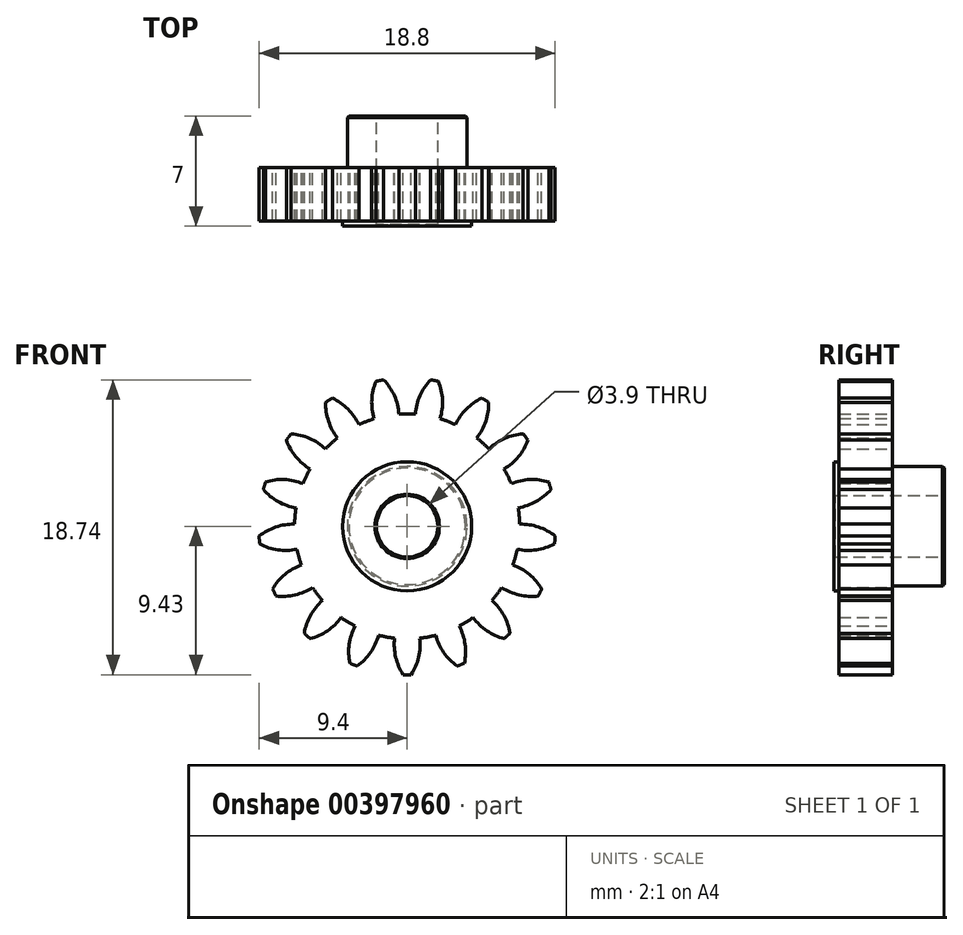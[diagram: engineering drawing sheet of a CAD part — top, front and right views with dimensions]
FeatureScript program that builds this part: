
annotation { "Feature Type Name" : "Feature", "Feature Type Description" : "" }
export const myFeature = defineFeature(function(context is Context, id is Id, definition is map)
    precondition{}
    {
        {
            var Q0;
            Q0=qCreatedBy(makeId("Front.planeOp"),FACE);
            var sketch = newSketch(context, id + "F0", { "sketchPlane" : qUnion([Q0])});
            skArc(sketch, "E0", {"start": v(-7.05, 1.17) * mm, "mid": v(-7.12, 0.66) * mm, "end": v(-7.15, 0.14) * mm});
            skLineSegment(sketch, "E1", {"start": v(-1.73, 9.26) * mm, "end": v(-1.31, 7.03) * mm});
            skLineSegment(sketch, "E2", {"start": v(1.73, 9.26) * mm, "end": v(1.31, 7.03) * mm});
            skLineSegment(sketch, "E3.1.0", {"start": v(9.06, 2.58) * mm, "end": v(6.88, 1.96) * mm});
            skLineSegment(sketch, "E3.1.1", {"start": v(9.38, -0.87) * mm, "end": v(7.12, -0.66) * mm});
            skArc(sketch, "E3.1.2", {"start": v(-7.37, 5.88) * mm, "mid": v(-7.52, 5.68) * mm, "end": v(-7.67, 5.48) * mm});
            skLineSegment(sketch, "E3.2.0", {"start": v(4.96, 8.01) * mm, "end": v(3.76, 6.08) * mm});
            skLineSegment(sketch, "E3.2.1", {"start": v(7.52, 5.68) * mm, "end": v(5.7, 4.3) * mm});
            skLineSegment(sketch, "E4.1.0", {"start": v(-8.44, -4.2) * mm, "end": v(-6.4, -3.19) * mm});
            skLineSegment(sketch, "E4.1.1", {"start": v(-9.38, -0.87) * mm, "end": v(-7.12, -0.66) * mm});
            skLineSegment(sketch, "E4.1.2", {"start": v(-9.07, 2.58) * mm, "end": v(-6.88, 1.96) * mm});
            skLineSegment(sketch, "E4.1.3", {"start": v(-7.52, 5.68) * mm, "end": v(-5.7, 4.3) * mm});
            skLineSegment(sketch, "E4.1.4", {"start": v(-4.96, 8.01) * mm, "end": v(-3.76, 6.08) * mm});
            skLineSegment(sketch, "E4.2.0", {"start": v(8.44, -4.2) * mm, "end": v(6.4, -3.19) * mm});
            skLineSegment(sketch, "E4.2.1", {"start": v(6.35, -6.96) * mm, "end": v(4.82, -5.28) * mm});
            skLineSegment(sketch, "E4.2.2", {"start": v(3.4, -8.79) * mm, "end": v(2.58, -6.67) * mm});
            skLineSegment(sketch, "E4.2.3", {"start": v(0, -9.42) * mm, "end": v(0, -7.15) * mm});
            skLineSegment(sketch, "E4.2.4", {"start": v(-3.4, -8.79) * mm, "end": v(-2.58, -6.67) * mm});
            skLineSegment(sketch, "E4.2.5", {"start": v(-6.35, -6.97) * mm, "end": v(-4.82, -5.28) * mm});
            skPoint(sketch, "E5", {"position": v(-2.1, 6.84) * mm});
            skPoint(sketch, "E6", {"position": v(0.52, 7.13) * mm});
            skPoint(sketch, "E7", {"position": v(3.06, 6.46) * mm});
            skPoint(sketch, "E8", {"position": v(5.19, 4.92) * mm});
            skPoint(sketch, "E9", {"position": v(6.61, 2.71) * mm});
            skPoint(sketch, "E10", {"position": v(6.72, -2.45) * mm});
            skPoint(sketch, "E11", {"position": v(5.38, -4.71) * mm});
            skPoint(sketch, "E12", {"position": v(3.31, -6.34) * mm});
            skPoint(sketch, "E13", {"position": v(0.8, -7.1) * mm});
            skPoint(sketch, "E14", {"position": v(-1.82, -6.91) * mm});
            skPoint(sketch, "E15", {"position": v(-4.2, -5.8) * mm});
            skPoint(sketch, "E16", {"position": v(-6, -3.88) * mm});
            skPoint(sketch, "E17", {"position": v(-7, -1.45) * mm});
            skPoint(sketch, "E18", {"position": v(-7.05, 1.17) * mm});
            skPoint(sketch, "E19", {"position": v(-6.15, 3.64) * mm});
            skPoint(sketch, "E20", {"position": v(-4.42, 5.62) * mm});
            skPoint(sketch, "E21", {"position": v(7.15, 0.14) * mm});
            skPoint(sketch, "E22", {"position": v(1.48, 9.3) * mm});
            skPoint(sketch, "E23", {"position": v(4.75, 8.14) * mm});
            skPoint(sketch, "E24", {"position": v(7.37, 5.88) * mm});
            skPoint(sketch, "E25", {"position": v(9, 2.82) * mm});
            skPoint(sketch, "E26", {"position": v(9.4, -0.62) * mm});
            skPoint(sketch, "E27", {"position": v(8.55, -3.97) * mm});
            skPoint(sketch, "E28", {"position": v(6.53, -6.8) * mm});
            skPoint(sketch, "E29", {"position": v(3.64, -8.7) * mm});
            skPoint(sketch, "E30", {"position": v(0.25, -9.42) * mm});
            skPoint(sketch, "E31", {"position": v(-3.17, -8.88) * mm});
            skPoint(sketch, "E32", {"position": v(-6.16, -7.13) * mm});
            skPoint(sketch, "E33", {"position": v(-8.32, -4.42) * mm});
            skPoint(sketch, "E34", {"position": v(-9.36, -1.12) * mm});
            skPoint(sketch, "E35", {"position": v(-9.13, 2.34) * mm});
            skPoint(sketch, "E36", {"position": v(-7.67, 5.48) * mm});
            skArc(sketch, "E37.MirrorCS", {"start": v(-1.98, 9.22) * mm, "mid": v(-2.24, 8.04) * mm, "end": v(-2.1, 6.84) * mm});
            skArc(sketch, "E38", {"start": v(1.48, 9.3) * mm, "mid": v(0.81, 8.3) * mm, "end": v(0.52, 7.13) * mm});
            skArc(sketch, "E39", {"start": v(4.75, 8.14) * mm, "mid": v(3.76, 7.45) * mm, "end": v(3.06, 6.46) * mm});
            skArc(sketch, "E40", {"start": v(7.37, 5.88) * mm, "mid": v(6.2, 5.6) * mm, "end": v(5.19, 4.92) * mm});
            skArc(sketch, "E41", {"start": v(9, 2.82) * mm, "mid": v(7.8, 2.98) * mm, "end": v(6.61, 2.71) * mm});
            skArc(sketch, "E42", {"start": v(9.4, -0.62) * mm, "mid": v(8.34, -0.04) * mm, "end": v(7.15, 0.14) * mm});
            skArc(sketch, "E43", {"start": v(8.55, -3.97) * mm, "mid": v(7.77, -3.05) * mm, "end": v(6.72, -2.45) * mm});
            skArc(sketch, "E44", {"start": v(6.53, -6.8) * mm, "mid": v(6.14, -5.65) * mm, "end": v(5.38, -4.71) * mm});
            skArc(sketch, "E45", {"start": v(3.64, -8.7) * mm, "mid": v(3.68, -7.49) * mm, "end": v(3.31, -6.34) * mm});
            skArc(sketch, "E46", {"start": v(0.25, -9.42) * mm, "mid": v(0.73, -8.31) * mm, "end": v(0.8, -7.1) * mm});
            skArc(sketch, "E47", {"start": v(-3.17, -8.88) * mm, "mid": v(-2.32, -8.01) * mm, "end": v(-1.82, -6.91) * mm});
            skArc(sketch, "E48", {"start": v(-6.16, -7.13) * mm, "mid": v(-5.06, -6.63) * mm, "end": v(-4.2, -5.8) * mm});
            skArc(sketch, "E49", {"start": v(-8.32, -4.42) * mm, "mid": v(-7.12, -4.36) * mm, "end": v(-6, -3.88) * mm});
            skArc(sketch, "E50", {"start": v(-9.36, -1.12) * mm, "mid": v(-8.2, -1.5) * mm, "end": v(-7, -1.45) * mm});
            skArc(sketch, "E51", {"start": v(-9.13, 2.34) * mm, "mid": v(-8.2, 1.57) * mm, "end": v(-7.05, 1.17) * mm});
            skArc(sketch, "E52", {"start": v(-7.67, 5.48) * mm, "mid": v(-7.07, 4.43) * mm, "end": v(-6.15, 3.64) * mm});
            skArc(sketch, "E53", {"start": v(-5.17, 7.88) * mm, "mid": v(-5, 6.68) * mm, "end": v(-4.42, 5.62) * mm});
            skArc(sketch, "E54.MirrorCS", {"start": v(-1.49, 9.3) * mm, "mid": v(-0.81, 8.3) * mm, "end": v(-0.52, 7.13) * mm});
            skArc(sketch, "E55.MirrorCS", {"start": v(1.98, 9.22) * mm, "mid": v(2.24, 8.04) * mm, "end": v(2.1, 6.84) * mm});
            skArc(sketch, "E56.MirrorCS", {"start": v(5.17, 7.88) * mm, "mid": v(5, 6.68) * mm, "end": v(4.42, 5.62) * mm});
            skArc(sketch, "E57.MirrorCS", {"start": v(7.67, 5.48) * mm, "mid": v(7.07, 4.43) * mm, "end": v(6.15, 3.64) * mm});
            skArc(sketch, "E58.MirrorCS", {"start": v(9.13, 2.34) * mm, "mid": v(8.2, 1.58) * mm, "end": v(7.05, 1.18) * mm});
            skArc(sketch, "E59.MirrorCS", {"start": v(9.36, -1.12) * mm, "mid": v(8.2, -1.5) * mm, "end": v(7, -1.45) * mm});
            skArc(sketch, "E60.MirrorCS", {"start": v(8.32, -4.42) * mm, "mid": v(7.12, -4.36) * mm, "end": v(6, -3.88) * mm});
            skArc(sketch, "E61.MirrorCS", {"start": v(6.16, -7.13) * mm, "mid": v(5.06, -6.63) * mm, "end": v(4.2, -5.79) * mm});
            skArc(sketch, "E62.MirrorCS", {"start": v(3.17, -8.88) * mm, "mid": v(2.32, -8.01) * mm, "end": v(1.82, -6.91) * mm});
            skArc(sketch, "E63.MirrorCS", {"start": v(-0.25, -9.42) * mm, "mid": v(-0.73, -8.31) * mm, "end": v(-0.8, -7.1) * mm});
            skArc(sketch, "E64.MirrorCS", {"start": v(-3.64, -8.7) * mm, "mid": v(-3.68, -7.49) * mm, "end": v(-3.31, -6.34) * mm});
            skArc(sketch, "E65.MirrorCS", {"start": v(-6.53, -6.8) * mm, "mid": v(-6.14, -5.65) * mm, "end": v(-5.38, -4.71) * mm});
            skArc(sketch, "E66.MirrorCS", {"start": v(-8.54, -3.98) * mm, "mid": v(-7.76, -3.05) * mm, "end": v(-6.72, -2.45) * mm});
            skArc(sketch, "E67.MirrorCS", {"start": v(-9.4, -0.62) * mm, "mid": v(-8.34, -0.04) * mm, "end": v(-7.15, 0.14) * mm});
            skArc(sketch, "E68.MirrorCS", {"start": v(-9, 2.82) * mm, "mid": v(-7.8, 2.97) * mm, "end": v(-6.62, 2.71) * mm});
            skArc(sketch, "E69.MirrorCS", {"start": v(-7.37, 5.88) * mm, "mid": v(-6.2, 5.59) * mm, "end": v(-5.19, 4.92) * mm});
            skArc(sketch, "E70.MirrorCS", {"start": v(-4.75, 8.14) * mm, "mid": v(-3.76, 7.45) * mm, "end": v(-3.06, 6.46) * mm});
            skLineSegment(sketch, "E71", {"start": v(9.13, 2.34) * mm, "end": v(9.4, -0.62) * mm, "construction": true});
            skPoint(sketch, "E72", {"position": v(9.27, 0.86) * mm});
            skArc(sketch, "E73.trimOffspring", {"start": v(-4.75, 8.14) * mm, "mid": v(-4.96, 8.01) * mm, "end": v(-5.17, 7.88) * mm});
            skArc(sketch, "E74.trimOffspring", {"start": v(-1.49, 9.3) * mm, "mid": v(-1.73, 9.26) * mm, "end": v(-1.98, 9.22) * mm});
            skArc(sketch, "E75.trimOffspring", {"start": v(1.98, 9.22) * mm, "mid": v(1.73, 9.26) * mm, "end": v(1.48, 9.3) * mm});
            skArc(sketch, "E76.trimOffspring", {"start": v(5.17, 7.88) * mm, "mid": v(4.96, 8.01) * mm, "end": v(4.75, 8.14) * mm});
            skArc(sketch, "E77.trimOffspring", {"start": v(7.67, 5.48) * mm, "mid": v(7.52, 5.68) * mm, "end": v(7.37, 5.88) * mm});
            skArc(sketch, "E78.trimOffspring", {"start": v(9.13, 2.34) * mm, "mid": v(9.06, 2.58) * mm, "end": v(9, 2.82) * mm});
            skArc(sketch, "E79.trimOffspring", {"start": v(9.36, -1.12) * mm, "mid": v(9.38, -0.87) * mm, "end": v(9.4, -0.62) * mm});
            skArc(sketch, "E80.trimOffspring", {"start": v(8.32, -4.42) * mm, "mid": v(8.44, -4.2) * mm, "end": v(8.55, -3.97) * mm});
            skArc(sketch, "E81.trimOffspring", {"start": v(6.16, -7.13) * mm, "mid": v(6.35, -6.96) * mm, "end": v(6.53, -6.8) * mm});
            skArc(sketch, "E82.trimOffspring", {"start": v(3.17, -8.88) * mm, "mid": v(3.4, -8.79) * mm, "end": v(3.64, -8.7) * mm});
            skArc(sketch, "E83.trimOffspring", {"start": v(-0.25, -9.42) * mm, "mid": v(0, -9.42) * mm, "end": v(0.25, -9.42) * mm});
            skArc(sketch, "E84.trimOffspring", {"start": v(-3.64, -8.7) * mm, "mid": v(-3.4, -8.79) * mm, "end": v(-3.17, -8.88) * mm});
            skArc(sketch, "E85.trimOffspring", {"start": v(-6.53, -6.8) * mm, "mid": v(-6.35, -6.97) * mm, "end": v(-6.16, -7.13) * mm});
            skArc(sketch, "E86.trimOffspring", {"start": v(-8.54, -3.98) * mm, "mid": v(-8.44, -4.2) * mm, "end": v(-8.32, -4.42) * mm});
            skArc(sketch, "E87.trimOffspring", {"start": v(-9.4, -0.62) * mm, "mid": v(-9.38, -0.87) * mm, "end": v(-9.36, -1.12) * mm});
            skArc(sketch, "E88.trimOffspring", {"start": v(-9, 2.82) * mm, "mid": v(-9.07, 2.58) * mm, "end": v(-9.13, 2.34) * mm});
            skArc(sketch, "E89.trimOffspring", {"start": v(-6.15, 3.64) * mm, "mid": v(-6.4, 3.19) * mm, "end": v(-6.62, 2.71) * mm});
            skArc(sketch, "E90.trimOffspring", {"start": v(-4.42, 5.62) * mm, "mid": v(-4.82, 5.28) * mm, "end": v(-5.19, 4.92) * mm});
            skArc(sketch, "E91.trimOffspring", {"start": v(-2.1, 6.84) * mm, "mid": v(-2.58, 6.67) * mm, "end": v(-3.06, 6.46) * mm});
            skArc(sketch, "E92.trimOffspring", {"start": v(0.52, 7.13) * mm, "mid": v(0, 7.15) * mm, "end": v(-0.52, 7.13) * mm});
            skArc(sketch, "E93.trimOffspring", {"start": v(3.06, 6.46) * mm, "mid": v(2.58, 6.67) * mm, "end": v(2.1, 6.84) * mm});
            skArc(sketch, "E94.trimOffspring", {"start": v(5.19, 4.92) * mm, "mid": v(4.82, 5.28) * mm, "end": v(4.42, 5.62) * mm});
            skArc(sketch, "E95.trimOffspring", {"start": v(6.61, 2.71) * mm, "mid": v(6.4, 3.19) * mm, "end": v(6.15, 3.64) * mm});
            skArc(sketch, "E96.trimOffspring", {"start": v(7.15, 0.14) * mm, "mid": v(7.12, 0.66) * mm, "end": v(7.05, 1.18) * mm});
            skArc(sketch, "E97.trimOffspring", {"start": v(6.72, -2.45) * mm, "mid": v(6.88, -1.96) * mm, "end": v(7, -1.45) * mm});
            skArc(sketch, "E98.trimOffspring", {"start": v(5.38, -4.71) * mm, "mid": v(5.7, -4.3) * mm, "end": v(6, -3.88) * mm});
            skArc(sketch, "E99.trimOffspring", {"start": v(3.31, -6.34) * mm, "mid": v(3.76, -6.08) * mm, "end": v(4.2, -5.79) * mm});
            skArc(sketch, "E100.trimOffspring", {"start": v(0.8, -7.1) * mm, "mid": v(1.31, -7.03) * mm, "end": v(1.82, -6.91) * mm});
            skArc(sketch, "E101.trimOffspring", {"start": v(-1.82, -6.91) * mm, "mid": v(-1.31, -7.03) * mm, "end": v(-0.8, -7.1) * mm});
            skArc(sketch, "E102.trimOffspring", {"start": v(-4.2, -5.8) * mm, "mid": v(-3.76, -6.08) * mm, "end": v(-3.31, -6.34) * mm});
            skArc(sketch, "E103.trimOffspring", {"start": v(-6, -3.88) * mm, "mid": v(-5.7, -4.3) * mm, "end": v(-5.38, -4.71) * mm});
            skArc(sketch, "E104.trimOffspring", {"start": v(-7, -1.45) * mm, "mid": v(-6.88, -1.96) * mm, "end": v(-6.72, -2.45) * mm});
            skCircle(sketch, "E105", {"center": v(0, 0) * mm, "radius": 1.95 * mm});
            skCircle(sketch, "E106", {"center": v(0, 0) * mm, "radius": 3.8 * mm});
            skCircle(sketch, "E107", {"center": v(0, 0) * mm, "radius": 4.1 * mm});
            skSolve(sketch);
        }
        {
            var Q0;
            Q0 = qSketchRegion(id + "F0", true);
            var Q1;
            Q1=makeQuery(id+"F0.imprint","IMPRINT",FACE,{"disambiguationData":[TD([[makeQuery(id+"F0.imprint","IMPRINT",EDGE,{"derivedFrom":sQuery(id+"F0.wireOp",EDGE,"pUOIDAn9-DAFQ-Yi0E-gMc4-7DeDaimTD4Ic")}),1.0]])]});
            extrude(context, id + "F1", {"entities" : qUnion([Q0, Q1]), "depth" : 3.4 * mm});
        }
        {
            var Q0;
            Q0=makeQuery(id+"F0.imprint","IMPRINT",FACE,{"disambiguationData":[TD([[makeQuery(id+"F0.imprint","IMPRINT",EDGE,{"derivedFrom":sQuery(id+"F0.wireOp",EDGE,"E105")}),-1.0]])]});
            extrude(context, id + "F2", {"entities" : qUnion([Q0]), "operationType" : NewBodyOperationType.ADD, "depth" : 3.72 * mm});
        }
        {
            var Q0;
            Q0=makeQuery(id+"F0.imprint","IMPRINT",FACE,{"disambiguationData":[TD([[makeQuery(id+"F0.imprint","IMPRINT",EDGE,{"derivedFrom":sQuery(id+"F0.wireOp",EDGE,"E105")}),-1.0]])]});
            extrude(context, id + "F3", {"entities" : qUnion([Q0]), "operationType" : NewBodyOperationType.ADD, "oppositeDirection" : true, "depth" : 3.28 * mm});
        }
        {
            var Q0;
            Q0=makeQuery(id+"F3.opExtrude","CAP_EDGE",EDGE,{"disambiguationData":[OSD([sQuery(id+"F0.wireOp",EDGE,"E105")])],"isStart":false});
            chamfer(context, id + "F4", {"entities" : qUnion([Q0]), "width" : 0.1 * mm, "tangentPropagation" : true});
        }
        {
            var Q0;
            Q0=makeQuery(id+"F2.opExtrude","CAP_EDGE",EDGE,{"disambiguationData":[OSD([sQuery(id+"F0.wireOp",EDGE,"E105")])],"isStart":false});
            chamfer(context, id + "F5", {"entities" : qUnion([Q0]), "width" : 0.1 * mm, "tangentPropagation" : true});
        }
        {
            var Q0;
            Q0=makeQuery(id+"F3.opExtrude","CAP_EDGE",EDGE,{"disambiguationData":[OSD([sQuery(id+"F0.wireOp",EDGE,"E106")])],"isStart":false});
            chamfer(context, id + "F6", {"entities" : qUnion([Q0]), "width" : 0.1 * mm, "tangentPropagation" : true});
        }
        {
            var Q0;
            Q0=makeQuery(id+"F0.imprint","IMPRINT",FACE,{"disambiguationData":[TD([[makeQuery(id+"F0.imprint","IMPRINT",EDGE,{"derivedFrom":sQuery(id+"F0.wireOp",EDGE,"E106")}),-1.0]])]});
            extrude(context, id + "F7", {"entities" : qUnion([Q0]), "operationType" : NewBodyOperationType.ADD, "depth" : 3.72 * mm});
        }
    });
